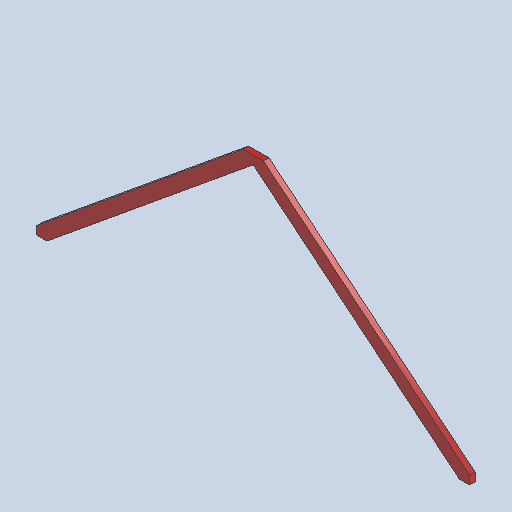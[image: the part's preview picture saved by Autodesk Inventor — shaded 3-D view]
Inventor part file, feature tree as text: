
AUTODESK INVENTOR PART (.ipt)
format: ipt  version: 2025 (Build 290162000, 162)  size: 101,376 bytes
history: native  units: in
note: dims shown in document units (in); Inventor stores cm internally (conversion verified against a paired STEP export)
features: other x4, sketch x1
ambient origin geometry x8: Origin, YZ Plane, XZ Plane, XY Plane, X Axis, Y Axis, Z Axis, Center Point
bodies: Solid1 (feature_tree)
feature tree (5):
  other  "side1.ipt"
  other  "Solid1::side1.ipt"
  other  "TaggingFeature1"
  sketch  "Sketch1"  dims[d0=0.3937in]
  other  "Finish1"
